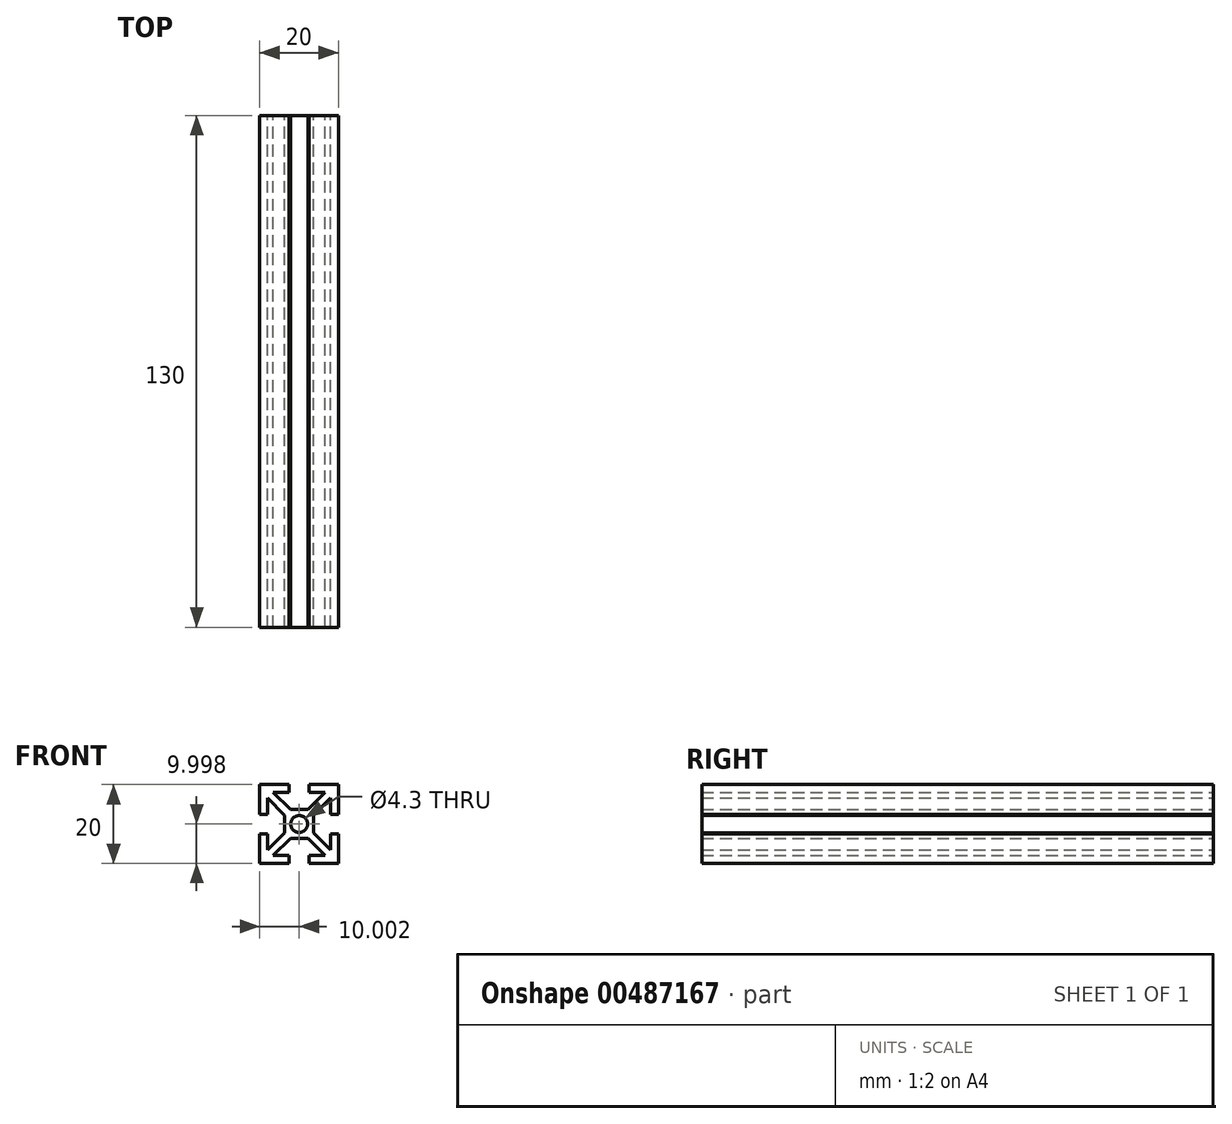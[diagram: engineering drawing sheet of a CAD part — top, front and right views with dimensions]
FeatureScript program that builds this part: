
annotation { "Feature Type Name" : "Feature", "Feature Type Description" : "" }
export const myFeature = defineFeature(function(context is Context, id is Id, definition is map)
    precondition{}
    {
        {
            var Q0;
            Q0=qCreatedBy(makeId("Front.planeOp"),FACE);
            var sketch = newSketch(context, id + "F0", { "sketchPlane" : qUnion([Q0])});
            skLineSegment(sketch, "E0.bottom", {"start": v(-9.74, 9.77) * mm, "end": v(-2.24, 9.77) * mm});
            skLineSegment(sketch, "E0.left", {"start": v(-9.74, 9.77) * mm, "end": v(-9.74, 2.27) * mm});
            skLineSegment(sketch, "E0.right", {"start": v(10.26, 9.77) * mm, "end": v(10.26, 2.27) * mm});
            skArc(sketch, "E1", {"start": v(2.41, -0.23) * mm, "mid": v(0.26, 1.92) * mm, "end": v(-1.89, -0.23) * mm});
            skLineSegment(sketch, "E2.bottom", {"start": v(-1.97, 3.42) * mm, "end": v(2.5, 3.42) * mm});
            skLineSegment(sketch, "E2.left", {"start": v(-3.39, 2) * mm, "end": v(-3.39, -0.23) * mm});
            skLineSegment(sketch, "E2.right", {"start": v(3.91, 2) * mm, "end": v(3.91, -0.23) * mm});
            skLineSegment(sketch, "E3", {"start": v(-2.24, 9.77) * mm, "end": v(-2.24, 7.77) * mm});
            skLineSegment(sketch, "E4", {"start": v(-2.24, 7.77) * mm, "end": v(-6.32, 7.77) * mm});
            skLineSegment(sketch, "E5", {"start": v(2.76, 9.77) * mm, "end": v(2.76, 7.77) * mm});
            skPoint(sketch, "E5.endSnap0", {"position": v(-5.99, 7.77) * mm});
            skLineSegment(sketch, "E6", {"start": v(2.76, 7.77) * mm, "end": v(6.85, 7.77) * mm});
            skLineSegment(sketch, "E7", {"start": v(-7.74, 6.35) * mm, "end": v(-7.74, 2.27) * mm});
            skLineSegment(sketch, "E8", {"start": v(-7.74, 2.27) * mm, "end": v(-9.74, 2.27) * mm});
            skLineSegment(sketch, "E9", {"start": v(-7.74, 6.35) * mm, "end": v(-3.39, 2) * mm});
            skLineSegment(sketch, "E10", {"start": v(-1.97, 3.42) * mm, "end": v(-6.32, 7.77) * mm});
            skPoint(sketch, "E10.endSnap0", {"position": v(-6.32, -0.18) * mm});
            skLineSegment(sketch, "E11", {"start": v(8.26, 6.35) * mm, "end": v(8.26, 2.27) * mm});
            skLineSegment(sketch, "E12", {"start": v(8.26, 2.27) * mm, "end": v(10.26, 2.27) * mm});
            skPoint(sketch, "E13.orphan", {"position": v(10.26, 7.77) * mm});
            skLineSegment(sketch, "E14", {"start": v(2.5, 3.42) * mm, "end": v(6.85, 7.77) * mm});
            skLineSegment(sketch, "E15", {"start": v(3.91, 2) * mm, "end": v(8.26, 6.35) * mm});
            skPoint(sketch, "E16.orphan", {"position": v(-9.74, 7.77) * mm});
            skPoint(sketch, "E17.orphan", {"position": v(-3.39, 3.42) * mm});
            skPoint(sketch, "E18.orphan", {"position": v(3.91, 3.42) * mm});
            skLineSegment(sketch, "E19", {"start": v(-9.74, -0.23) * mm, "end": v(10.26, -0.23) * mm, "construction": true});
            skPoint(sketch, "E0.top.end.orphan", {"position": v(10.26, -10.23) * mm});
            skPoint(sketch, "E0.top.start.orphan", {"position": v(-9.74, -10.23) * mm});
            skLineSegment(sketch, "E20.MirrorCS", {"start": v(-9.74, -10.23) * mm, "end": v(-9.74, -2.73) * mm});
            skLineSegment(sketch, "E21.MirrorCS", {"start": v(-7.74, -2.73) * mm, "end": v(-9.74, -2.73) * mm});
            skLineSegment(sketch, "E22.MirrorCS", {"start": v(-7.74, -6.82) * mm, "end": v(-7.74, -2.73) * mm});
            skLineSegment(sketch, "E23.MirrorCS", {"start": v(-7.74, -6.82) * mm, "end": v(-3.39, -2.47) * mm});
            skLineSegment(sketch, "E24.MirrorCS", {"start": v(-3.39, -2.47) * mm, "end": v(-3.39, -0.23) * mm});
            skArc(sketch, "E25.MirrorCS", {"start": v(2.41, -0.23) * mm, "mid": v(0.26, -2.38) * mm, "end": v(-1.89, -0.23) * mm});
            skLineSegment(sketch, "E26.MirrorCS", {"start": v(-1.97, -3.88) * mm, "end": v(-6.32, -8.23) * mm});
            skLineSegment(sketch, "E27.MirrorCS", {"start": v(-1.97, -3.88) * mm, "end": v(2.5, -3.88) * mm});
            skLineSegment(sketch, "E28.MirrorCS", {"start": v(-2.24, -8.23) * mm, "end": v(-6.32, -8.23) * mm});
            skLineSegment(sketch, "E29.MirrorCS", {"start": v(-2.24, -10.23) * mm, "end": v(-2.24, -8.23) * mm});
            skLineSegment(sketch, "E30.MirrorCS", {"start": v(-9.74, -10.23) * mm, "end": v(-2.24, -10.23) * mm});
            skLineSegment(sketch, "E31.MirrorCS", {"start": v(2.76, -10.23) * mm, "end": v(2.76, -8.23) * mm});
            skLineSegment(sketch, "E32.MirrorCS", {"start": v(2.76, -8.23) * mm, "end": v(6.85, -8.23) * mm});
            skLineSegment(sketch, "E33.MirrorCS", {"start": v(2.5, -3.88) * mm, "end": v(6.85, -8.23) * mm});
            skLineSegment(sketch, "E34.MirrorCS", {"start": v(3.91, -2.47) * mm, "end": v(8.26, -6.82) * mm});
            skLineSegment(sketch, "E35.MirrorCS", {"start": v(8.26, -6.82) * mm, "end": v(8.26, -2.73) * mm});
            skLineSegment(sketch, "E36.MirrorCS", {"start": v(8.26, -2.73) * mm, "end": v(10.26, -2.73) * mm});
            skLineSegment(sketch, "E37.MirrorCS", {"start": v(10.26, -10.23) * mm, "end": v(10.26, -2.73) * mm});
            skLineSegment(sketch, "E38.MirrorCS", {"start": v(3.91, -2.47) * mm, "end": v(3.91, -0.23) * mm});
            skLineSegment(sketch, "E39.trimOffspring", {"start": v(2.76, 9.77) * mm, "end": v(10.26, 9.77) * mm});
            skLineSegment(sketch, "E40.trimOffspring", {"start": v(2.76, -10.23) * mm, "end": v(10.26, -10.23) * mm});
            skSolve(sketch);
        }
        {
            var Q0;
            Q0=makeQuery(id+"F0.imprint","IMPRINT",FACE,{"disambiguationData":[TD([[makeQuery(id+"F0.imprint","IMPRINT",EDGE,{"derivedFrom":sQuery(id+"F0.wireOp",EDGE,"E0.bottom")}),-1.0]])]});
            extrude(context, id + "F1", {"entities" : qUnion([Q0]), "depth" : 65 * mm, "hasSecondDirection" : true, "secondDirectionOppositeDirection" : true, "secondDirectionDepth" : 65 * mm});
        }
    });
